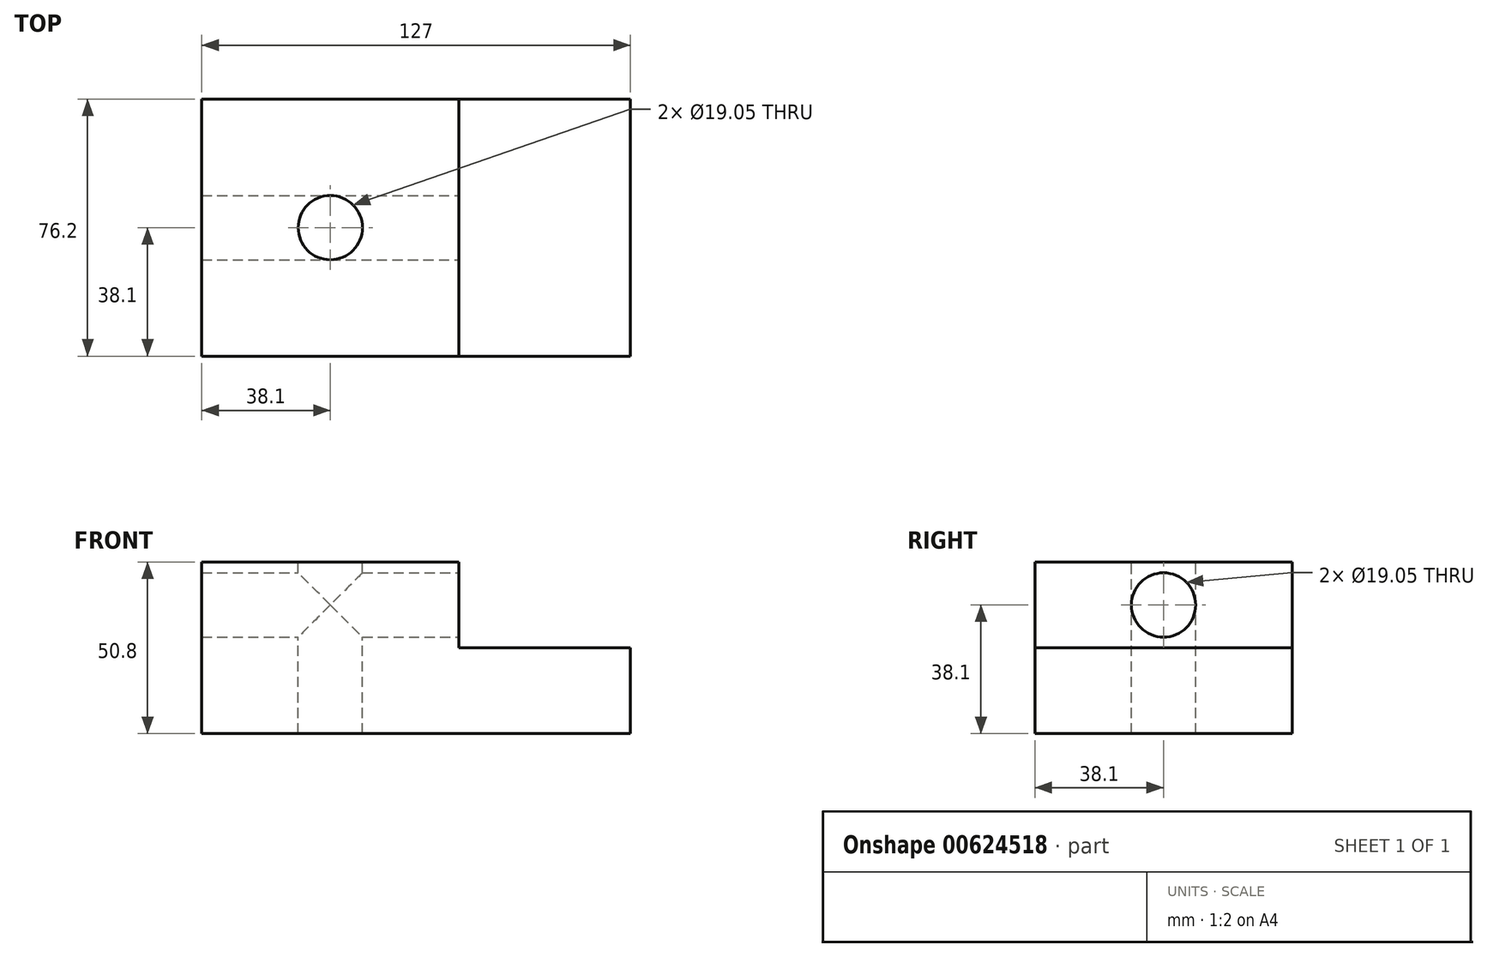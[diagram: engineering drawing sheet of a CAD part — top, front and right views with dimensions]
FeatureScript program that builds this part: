
annotation { "Feature Type Name" : "Feature", "Feature Type Description" : "" }
export const myFeature = defineFeature(function(context is Context, id is Id, definition is map)
    precondition{}
    {
        {
            var Q0;
            Q0=qCreatedBy(makeId("Front.planeOp"),FACE);
            var sketch = newSketch(context, id + "F0", { "sketchPlane" : qUnion([Q0])});
            skLineSegment(sketch, "E0.bottom", {"start": v(0, 0) * mm, "end": v(127, 0) * mm});
            skLineSegment(sketch, "E0.top", {"start": v(0, 50.8) * mm, "end": v(127, 50.8) * mm});
            skLineSegment(sketch, "E0.left", {"start": v(0, 0) * mm, "end": v(0, 50.8) * mm});
            skLineSegment(sketch, "E0.right", {"start": v(127, 0) * mm, "end": v(127, 50.8) * mm});
            skPoint(sketch, "E1.endSnap0", {"position": v(0, 25.4) * mm});
            skLineSegment(sketch, "E2", {"start": v(127, 25.4) * mm, "end": v(76.2, 25.4) * mm});
            skLineSegment(sketch, "E3", {"start": v(76.2, 25.4) * mm, "end": v(76.2, 50.8) * mm});
            skSolve(sketch);
        }
        {
            var Q0;
            {var subQ1=sQuery(id+"F0.wireOp",EDGE,"E0.bottom");Q0=makeQuery(id+"F0.imprint","IMPRINT",FACE,{"disambiguationData":[TD([[makeQuery(id+"F0.imprint","IMPRINT",EDGE,{"derivedFrom":subQ1}),1.0]])]});}
            extrude(context, id + "F1", {"entities" : qUnion([Q0]), "depth" : 76.2 * mm, "offsetDistance" : 25.4 * mm});
        }
        {
            var Q0;
            Q0=makeQuery(id+"F1.opExtrude","SWEPT_FACE",FACE,{"disambiguationData":[OSD([sQuery(id+"F0.wireOp",EDGE,"E0.top")])]});
            var sketch = newSketch(context, id + "F2", { "sketchPlane" : qUnion([Q0])});
            skPoint(sketch, "E4", {"position": v(38.1, -38.1) * mm});
            skPoint(sketch, "E4.positionSnap0", {"position": v(38.1, 0) * mm});
            skPoint(sketch, "E4.positionSnap1", {"position": v(0, -38.1) * mm});
            skSolve(sketch);
        }
        {
            var Q0;
            Q0=sQuery(id+"F2.wireOp",VERTEX,"E4");
            var Q1;
            Q1=makeQuery(id+"F1.opExtrude","SWEPT_BODY",BODY,{"disambiguationData":[OSD([sQuery(id+"F0.wireOp",EDGE,"E0.bottom"),sQuery(id+"F0.wireOp",EDGE,"E0.top"),sQuery(id+"F0.wireOp",EDGE,"E0.left"),sQuery(id+"F0.wireOp",EDGE,"E0.right"),sQuery(id+"F0.wireOp",EDGE,"E2"),sQuery(id+"F0.wireOp",EDGE,"E3")])]});
            hole(context, id + "F3", {"style" : HoleStyle.SIMPLE, "endStyle" : HoleEndStyle.THROUGH, "holeDiameter" : 19.05 * mm, "majorDiameter" : 6.35 * mm, "isTappedThrough" : true, "tappedDepth" : 12.7 * mm, "tapClearance" : 3, "locations" : qUnion([Q0]), "scope" : qUnion([Q1])});
        }
        {
            var Q0;
            Q0=makeQuery(id+"F1.opExtrude","SWEPT_FACE",FACE,{"disambiguationData":[OSD([sQuery(id+"F0.wireOp",EDGE,"E3")])]});
            var sketch = newSketch(context, id + "F4", { "sketchPlane" : qUnion([Q0])});
            skPoint(sketch, "E5", {"position": v(-38.1, 38.1) * mm});
            skPoint(sketch, "E5.positionSnap0", {"position": v(-38.1, 50.8) * mm});
            skPoint(sketch, "E5.positionSnap1", {"position": v(-76.2, 38.1) * mm});
            skSolve(sketch);
        }
        {
            var Q0;
            Q0=sQuery(id+"F4.wireOp",VERTEX,"E5");
            var Q1;
            Q1=makeQuery(id+"F1.opExtrude","SWEPT_BODY",BODY,{"disambiguationData":[OSD([sQuery(id+"F0.wireOp",EDGE,"E0.bottom"),sQuery(id+"F0.wireOp",EDGE,"E0.top"),sQuery(id+"F0.wireOp",EDGE,"E0.left"),sQuery(id+"F0.wireOp",EDGE,"E0.right"),sQuery(id+"F0.wireOp",EDGE,"E2"),sQuery(id+"F0.wireOp",EDGE,"E3")])]});
            hole(context, id + "F5", {"style" : HoleStyle.SIMPLE, "endStyle" : HoleEndStyle.THROUGH, "holeDiameter" : 19.05 * mm, "majorDiameter" : 6.35 * mm, "isTappedThrough" : true, "tappedDepth" : 12.7 * mm, "tapClearance" : 3, "locations" : qUnion([Q0]), "scope" : qUnion([Q1])});
        }
    });
